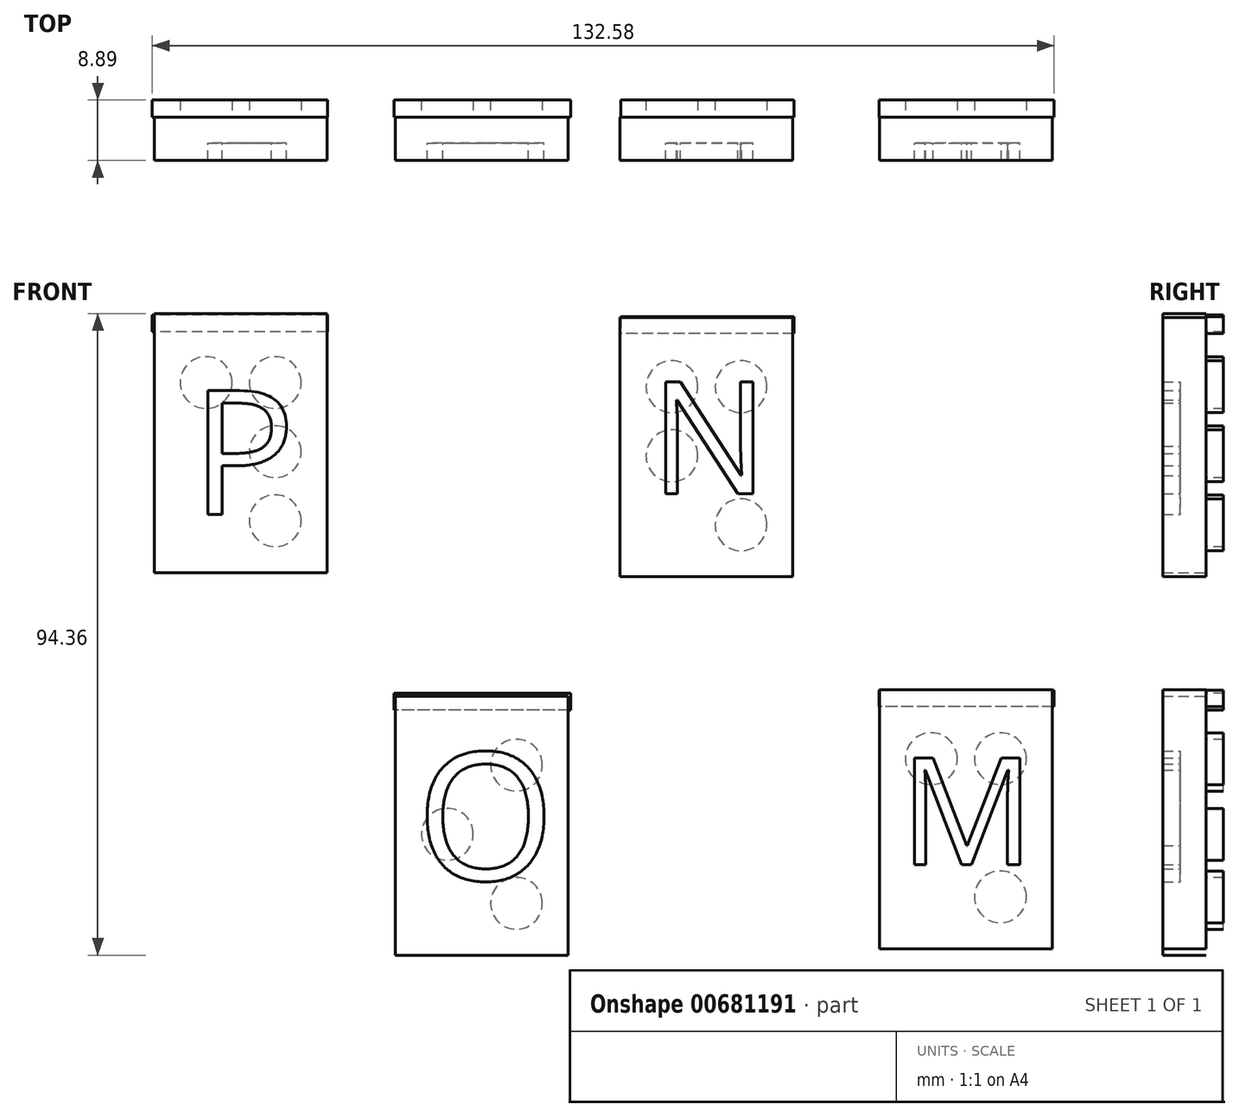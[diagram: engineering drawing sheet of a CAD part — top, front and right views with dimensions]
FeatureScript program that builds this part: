
annotation { "Feature Type Name" : "Feature", "Feature Type Description" : "" }
export const myFeature = defineFeature(function(context is Context, id is Id, definition is map)
    precondition{}
    {
        {
            var Q0;
            Q0=qCreatedBy(makeId("Front.planeOp"),FACE);
            var sketch = newSketch(context, id + "F0", { "sketchPlane" : qUnion([Q0])});
            skLineSegment(sketch, "E0.bottom", {"start": v(-58.76, 38.35) * mm, "end": v(-33.36, 38.35) * mm});
            skLineSegment(sketch, "E0.top", {"start": v(-58.76, 0.25) * mm, "end": v(-33.36, 0.25) * mm});
            skLineSegment(sketch, "E0.left", {"start": v(-58.76, 38.35) * mm, "end": v(-58.76, 0.25) * mm});
            skLineSegment(sketch, "E0.right", {"start": v(-33.36, 38.35) * mm, "end": v(-33.36, 0.25) * mm});
            skLineSegment(sketch, "E1.bottom", {"start": v(-23.3, -17.91) * mm, "end": v(2.1, -17.91) * mm});
            skLineSegment(sketch, "E1.top", {"start": v(-23.3, -56.01) * mm, "end": v(2.1, -56.01) * mm});
            skLineSegment(sketch, "E1.left", {"start": v(-23.3, -17.91) * mm, "end": v(-23.3, -56.01) * mm});
            skLineSegment(sketch, "E1.right", {"start": v(2.1, -17.91) * mm, "end": v(2.1, -56.01) * mm});
            skLineSegment(sketch, "E2.bottom", {"start": v(47.85, -16.96) * mm, "end": v(73.25, -16.96) * mm});
            skLineSegment(sketch, "E2.top", {"start": v(47.85, -55.06) * mm, "end": v(73.25, -55.06) * mm});
            skLineSegment(sketch, "E2.left", {"start": v(47.85, -16.96) * mm, "end": v(47.85, -55.06) * mm});
            skLineSegment(sketch, "E2.right", {"start": v(73.25, -16.96) * mm, "end": v(73.25, -55.06) * mm});
            skLineSegment(sketch, "E3.bottom", {"start": v(9.7, 37.75) * mm, "end": v(35.1, 37.75) * mm});
            skLineSegment(sketch, "E3.top", {"start": v(9.7, -0.35) * mm, "end": v(35.1, -0.35) * mm});
            skLineSegment(sketch, "E3.left", {"start": v(9.7, 37.75) * mm, "end": v(9.7, -0.35) * mm});
            skLineSegment(sketch, "E3.right", {"start": v(35.1, 37.75) * mm, "end": v(35.1, -0.35) * mm});
            skSolve(sketch);
        }
        {
            var Q0;
            Q0=qSketchRegion(id+"F0",true);
            extrude(context, id + "F1", {"entities" : qUnion([Q0]), "depth" : 6.35 * mm});
        }
        {
            var Q0;
            Q0=qCreatedBy(makeId("Front.planeOp"),FACE);
            var sketch = newSketch(context, id + "F2", { "sketchPlane" : qUnion([Q0])});
            skCircle(sketch, "E4", {"center": v(27.49, 7.27) * mm, "radius": 3.81 * mm});
            skCircle(sketch, "E5", {"center": v(65.63, -27.12) * mm, "radius": 3.81 * mm});
            skCircle(sketch, "E6", {"center": v(65.63, -47.44) * mm, "radius": 3.81 * mm});
            skCircle(sketch, "E7", {"center": v(-5.52, -28.07) * mm, "radius": 3.81 * mm});
            skCircle(sketch, "E8", {"center": v(27.49, 27.59) * mm, "radius": 3.81 * mm});
            skCircle(sketch, "E9", {"center": v(17.33, 27.59) * mm, "radius": 3.81 * mm});
            skCircle(sketch, "E10", {"center": v(-5.52, -48.4) * mm, "radius": 3.8 * mm});
            skCircle(sketch, "E11", {"center": v(-40.98, 28.19) * mm, "radius": 3.81 * mm});
            skCircle(sketch, "E12", {"center": v(-51.14, 28.19) * mm, "radius": 3.81 * mm});
            skCircle(sketch, "E13", {"center": v(-40.98, 18.03) * mm, "radius": 3.81 * mm});
            skCircle(sketch, "E14", {"center": v(-40.98, 7.87) * mm, "radius": 3.81 * mm});
            skCircle(sketch, "E15", {"center": v(55.47, -27.12) * mm, "radius": 3.81 * mm});
            skCircle(sketch, "E16", {"center": v(-15.68, -38.23) * mm, "radius": 3.81 * mm});
            skCircle(sketch, "E17", {"center": v(17.33, 17.43) * mm, "radius": 3.81 * mm});
            skSolve(sketch);
        }
        {
            var Q0;
            Q0=qSketchRegion(id+"F2",true);
            extrude(context, id + "F3", {"entities" : qUnion([Q0]), "operationType" : NewBodyOperationType.ADD, "oppositeDirection" : true, "depth" : 2.54 * mm});
        }
        {
            var Q0;
            Q0=qCreatedBy(makeId("Front.planeOp"),FACE);
            cPlane(context, id + "F4", {"entities" : qUnion([Q0]), "cplaneType" : CPlaneType.OFFSET, "offset" : 3.8 * mm, "width" : 152.4 * mm, "height" : 152.4 * mm});
        }
        {
            var Q0;
            Q0=qCreatedBy(id+"F4.planeOp",FACE);
            var sketch = newSketch(context, id + "F5", { "sketchPlane" : qUnion([Q0])});
            skText(sketch, "E18", { "text": "M", "fontName": "OpenSans-Regular.ttf"});
            skText(sketch, "E19", { "text": "N", "fontName": "OpenSans-Regular.ttf"});
            skText(sketch, "E20", { "text": "O", "fontName": "OpenSans-Regular.ttf"});
            skText(sketch, "E21", { "text": "P", "fontName": "OpenSans-Regular.ttf"});
            const initialGuessF5  = {"E18": [0.05083, -0.04268, 1, 0, 0.0158], "E19": [0.01414, 0.01185, 1, 0, 0.01656], "E20": [-0.02026, -0.04497, 1, 0, 0.01886], "E21": [-0.05338, 0.0088, 1, 0, 0.01835]};
            skSetInitialGuess(sketch, initialGuessF5);
            skSolve(sketch);
        }
        {
            var Q0;
            Q0=qSketchRegion(id+"F5",true);
            extrude(context, id + "F6", {"entities" : qUnion([Q0]), "operationType" : NewBodyOperationType.REMOVE, "depth" : 25.4 * mm});
        }
        {
            var Q0;
            Q0=qCreatedBy(makeId("Front.planeOp"),FACE);
            var sketch = newSketch(context, id + "F7", { "sketchPlane" : qUnion([Q0])});
            skLineSegment(sketch, "E22.bottom", {"start": v(73.52, -17.03) * mm, "end": v(47.79, -17.03) * mm});
            skLineSegment(sketch, "E22.top", {"start": v(73.52, -19.48) * mm, "end": v(47.79, -19.48) * mm});
            skLineSegment(sketch, "E22.left", {"start": v(73.52, -17.03) * mm, "end": v(73.52, -19.48) * mm});
            skLineSegment(sketch, "E22.right", {"start": v(47.79, -17.03) * mm, "end": v(47.79, -19.48) * mm});
            skLineSegment(sketch, "E23.bottom", {"start": v(35.29, 37.86) * mm, "end": v(9.8, 37.86) * mm});
            skLineSegment(sketch, "E23.top", {"start": v(35.29, 35.41) * mm, "end": v(9.8, 35.41) * mm});
            skLineSegment(sketch, "E23.left", {"start": v(35.29, 37.86) * mm, "end": v(35.29, 35.41) * mm});
            skLineSegment(sketch, "E23.right", {"start": v(9.8, 37.86) * mm, "end": v(9.8, 35.41) * mm});
            skLineSegment(sketch, "E24.bottom", {"start": v(-33.33, 38.1) * mm, "end": v(-59.06, 38.1) * mm});
            skLineSegment(sketch, "E24.top", {"start": v(-33.33, 35.66) * mm, "end": v(-59.06, 35.66) * mm});
            skLineSegment(sketch, "E24.left", {"start": v(-33.33, 38.1) * mm, "end": v(-33.33, 35.66) * mm});
            skLineSegment(sketch, "E24.right", {"start": v(-59.06, 38.1) * mm, "end": v(-59.06, 35.66) * mm});
            skLineSegment(sketch, "E25.bottom", {"start": v(2.45, -17.52) * mm, "end": v(-23.53, -17.52) * mm});
            skLineSegment(sketch, "E25.top", {"start": v(2.45, -19.97) * mm, "end": v(-23.53, -19.97) * mm});
            skLineSegment(sketch, "E25.left", {"start": v(2.45, -17.52) * mm, "end": v(2.45, -19.97) * mm});
            skLineSegment(sketch, "E25.right", {"start": v(-23.53, -17.52) * mm, "end": v(-23.53, -19.97) * mm});
            skSolve(sketch);
        }
        {
            var Q0;
            Q0=qSketchRegion(id+"F7",true);
            extrude(context, id + "F8", {"entities" : qUnion([Q0]), "operationType" : NewBodyOperationType.ADD, "oppositeDirection" : true, "depth" : 2.54 * mm});
        }
    });
